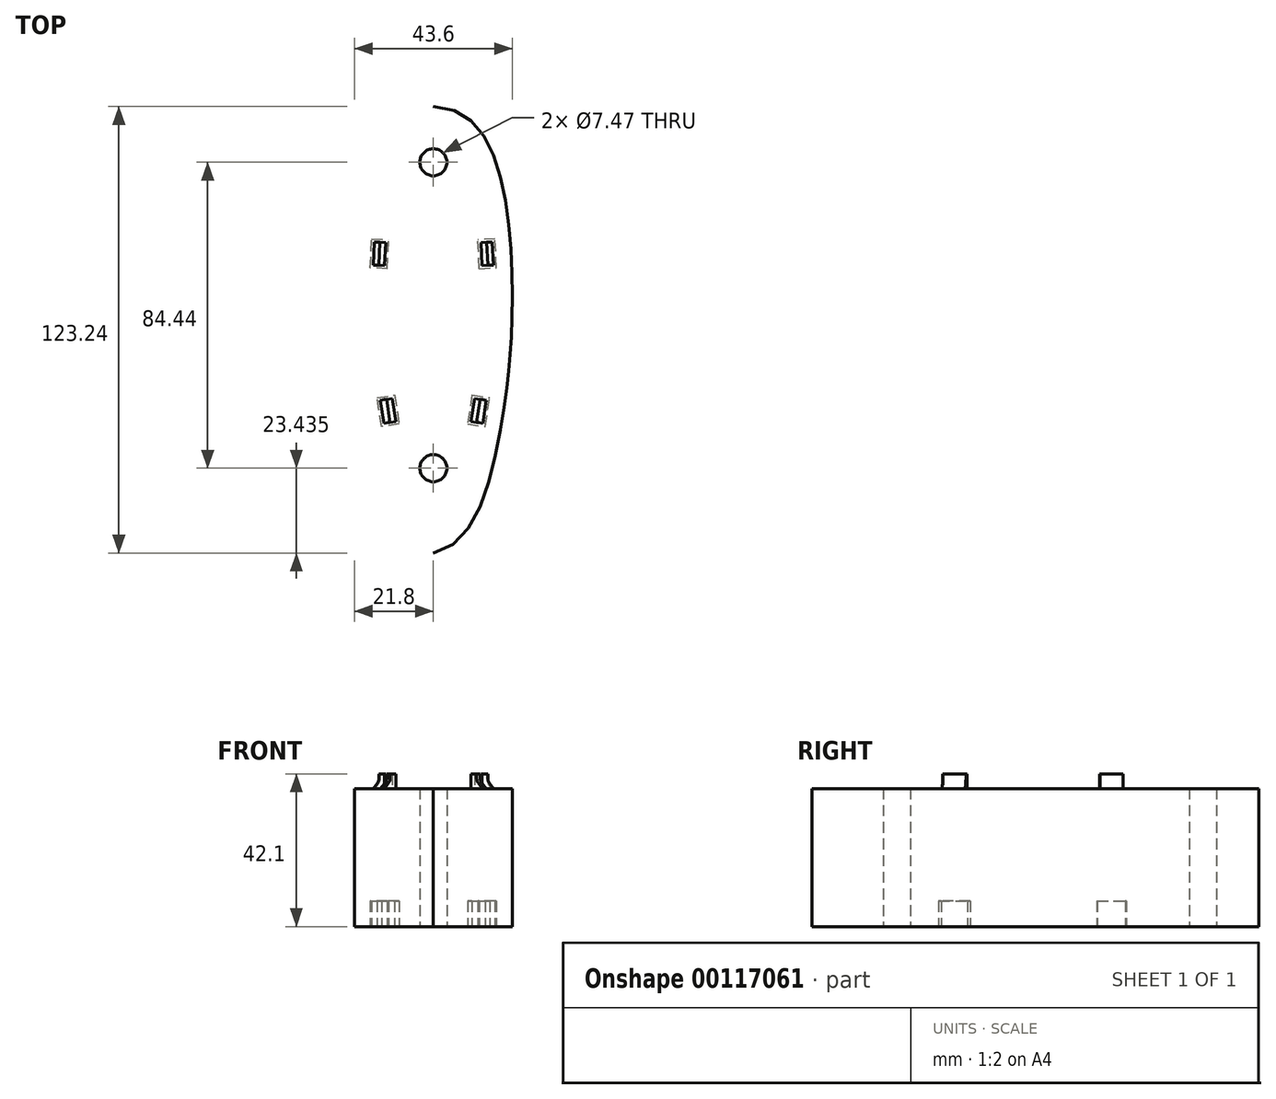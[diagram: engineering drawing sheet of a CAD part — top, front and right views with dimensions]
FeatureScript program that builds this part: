
annotation { "Feature Type Name" : "Feature", "Feature Type Description" : "" }
export const myFeature = defineFeature(function(context is Context, id is Id, definition is map)
    precondition{}
    {
        {
            var Q0;
            Q0=qCreatedBy(makeId("Top.planeOp"),FACE);
            var sketch = newSketch(context, id + "F0", { "sketchPlane" : qUnion([Q0])});
            skPoint(sketch, "E0", {"position": v(0, -61.62) * mm});
            skPoint(sketch, "E1", {"position": v(0, 61.62) * mm});
            skLineSegment(sketch, "E2", {"start": v(0, 71.88) * mm, "end": v(0, 61.62) * mm, "construction": true});
            skLineSegment(sketch, "E3", {"start": v(0, -61.62) * mm, "end": v(0, -68.33) * mm, "construction": true});
            skLineSegment(sketch, "E4", {"start": v(0, 61.62) * mm, "end": v(0, -61.62) * mm, "construction": true});
            skLineSegment(sketch, "E5", {"start": v(-21.58, 0) * mm, "end": v(21.58, 0) * mm, "construction": true});
            skSolve(sketch);
        }
        {
            var Q0;
            Q0=qCreatedBy(makeId("Top.planeOp"),FACE);
            var sketch = newSketch(context, id + "F1", { "sketchPlane" : qUnion([Q0])});
            skPoint(sketch, "E6.0", {"position": v(0, -61.62) * mm});
            skPoint(sketch, "E7.0", {"position": v(-21.58, 0) * mm});
            skPoint(sketch, "E8.0", {"position": v(0, 61.62) * mm});
            skPoint(sketch, "E9.0", {"position": v(21.58, 0) * mm});
            skFitSpline(sketch, "E10", {"points": [v(0, 61.62) * mm, v(-18.98, 40.1) * mm, v(-21.58, 0) * mm, v(-18.86, -25.18) * mm, v(0, -61.62) * mm], "startDerivative": vector(-149.62, -2.8) * mm, "endDerivative": vector(137.56, -24.42) * mm});
            skLineSegment(sketch, "E11.0", {"start": v(0, 61.62) * mm, "end": v(0, -61.62) * mm, "construction": true});
            skFitSpline(sketch, "E12.MirrorCS", {"points": [v(0, 61.62) * mm, v(18.98, 40.1) * mm, v(21.58, 0) * mm, v(18.86, -25.18) * mm, v(0, -61.62) * mm], "startDerivative": vector(149.62, -2.8) * mm, "endDerivative": vector(-137.56, -24.42) * mm});
            skCircle(sketch, "E13", {"center": v(0, 46.26) * mm, "radius": 2.94 * mm});
            skLineSegment(sketch, "E14", {"start": v(0, 49.2) * mm, "end": v(0, 61.62) * mm, "construction": true});
            skCircle(sketch, "E15", {"center": v(0, -38.18) * mm, "radius": 2.94 * mm});
            skLineSegment(sketch, "E16", {"start": v(0, -61.62) * mm, "end": v(0, -41.12) * mm, "construction": true});
            skFitSpline(sketch, "E17.0", {"points": [v(0.1, 56.52) * mm, v(-1.07, 56.5) * mm, v(-2.58, 56.27) * mm, v(-4.26, 55.69) * mm, v(-5.4, 55.12) * mm, v(-6.45, 54.4) * mm, v(-7.79, 53.23) * mm, v(-9.34, 51.35) * mm, v(-11, 48.38) * mm, v(-12.44, 44.8) * mm, v(-13.42, 41.44) * mm, v(-14.1, 38.58) * mm, v(-14.72, 35.65) * mm, v(-15.35, 31.88) * mm, v(-16.11, 25.7) * mm, v(-16.53, 19.45) * mm, v(-16.7, 13.37) * mm, v(-16.71, 8.96) * mm, v(-16.66, 5.46) * mm, v(-16.58, 2.8) * mm, v(-16.51, 0.86) * mm, v(-16.43, -0.98) * mm, v(-16.32, -3.32) * mm, v(-16.15, -6.08) * mm, v(-15.88, -9.27) * mm, v(-15.55, -12.48) * mm, v(-15.13, -15.85) * mm, v(-14.6, -19.52) * mm, v(-14.06, -22.95) * mm, v(-13.56, -25.98) * mm, v(-13, -29.14) * mm, v(-12.22, -33.28) * mm, v(-11.05, -38.32) * mm, v(-9.62, -43.18) * mm, v(-7.9, -47.62) * mm, v(-5.9, -51.36) * mm, v(-4.07, -53.7) * mm, v(-2.58, -55.03) * mm, v(-1.47, -55.78) * mm, v(-0.34, -56.3) * mm, v(0.46, -56.52) * mm, v(0.9, -56.6) * mm], "construction": true});
            skFitSpline(sketch, "E18.0", {"points": [v(-0.1, 56.52) * mm, v(1.07, 56.5) * mm, v(2.58, 56.27) * mm, v(4.26, 55.69) * mm, v(5.4, 55.12) * mm, v(6.45, 54.4) * mm, v(7.79, 53.23) * mm, v(9.34, 51.35) * mm, v(11, 48.38) * mm, v(12.44, 44.8) * mm, v(13.42, 41.44) * mm, v(14.1, 38.58) * mm, v(14.72, 35.65) * mm, v(15.35, 31.88) * mm, v(16.11, 25.7) * mm, v(16.53, 19.45) * mm, v(16.7, 13.37) * mm, v(16.71, 8.96) * mm, v(16.66, 5.46) * mm, v(16.58, 2.8) * mm, v(16.51, 0.86) * mm, v(16.43, -0.98) * mm, v(16.32, -3.32) * mm, v(16.15, -6.08) * mm, v(15.88, -9.27) * mm, v(15.55, -12.48) * mm, v(15.13, -15.85) * mm, v(14.6, -19.52) * mm, v(14.06, -22.95) * mm, v(13.56, -25.98) * mm, v(13, -29.14) * mm, v(12.22, -33.28) * mm, v(11.05, -38.32) * mm, v(9.62, -43.18) * mm, v(7.9, -47.62) * mm, v(5.9, -51.36) * mm, v(4.07, -53.7) * mm, v(2.58, -55.03) * mm, v(1.47, -55.78) * mm, v(0.34, -56.3) * mm, v(-0.46, -56.52) * mm, v(-0.9, -56.6) * mm], "construction": true});
            skLineSegment(sketch, "E19", {"start": v(-13.46, 17.73) * mm, "end": v(13.46, 17.73) * mm, "construction": true});
            skLineSegment(sketch, "E20", {"start": v(-11.32, -18.93) * mm, "end": v(11.32, -18.93) * mm, "construction": true});
            skPoint(sketch, "E21", {"position": v(0, -18.93) * mm});
            skLineSegment(sketch, "E22", {"start": v(-10.36, -25.3) * mm, "end": v(10.36, -25.3) * mm, "construction": true});
            skPoint(sketch, "E23", {"position": v(0, -25.3) * mm});
            skLineSegment(sketch, "E24", {"start": v(-11.32, -18.93) * mm, "end": v(-10.36, -25.3) * mm});
            skLineSegment(sketch, "E25", {"start": v(-11.32, -18.93) * mm, "end": v(-14.6, -19.42) * mm});
            skLineSegment(sketch, "E26", {"start": v(-14.6, -19.42) * mm, "end": v(-13.64, -25.8) * mm});
            skLineSegment(sketch, "E27", {"start": v(-15.51, -18.75) * mm, "end": v(-10.65, -18.02) * mm});
            skLineSegment(sketch, "E28", {"start": v(-14.31, -26.7) * mm, "end": v(-15.51, -18.75) * mm});
            skLineSegment(sketch, "E29", {"start": v(-10.65, -18.02) * mm, "end": v(-15.51, -18.75) * mm});
            skLineSegment(sketch, "E30", {"start": v(-10.65, -18.02) * mm, "end": v(-9.45, -25.97) * mm});
            skLineSegment(sketch, "E31", {"start": v(-9.45, -25.97) * mm, "end": v(-14.31, -26.7) * mm});
            skLineSegment(sketch, "E32.MirrorCS", {"start": v(10.65, -18.02) * mm, "end": v(9.45, -25.97) * mm});
            skLineSegment(sketch, "E33.MirrorCS", {"start": v(11.32, -18.93) * mm, "end": v(10.36, -25.3) * mm});
            skLineSegment(sketch, "E34.MirrorCS", {"start": v(9.45, -25.97) * mm, "end": v(14.31, -26.7) * mm});
            skLineSegment(sketch, "E35.MirrorCS", {"start": v(10.36, -25.3) * mm, "end": v(13.64, -25.8) * mm});
            skLineSegment(sketch, "E36.MirrorCS", {"start": v(11.32, -18.93) * mm, "end": v(14.6, -19.42) * mm});
            skLineSegment(sketch, "E37.MirrorCS", {"start": v(10.65, -18.02) * mm, "end": v(15.51, -18.75) * mm});
            skLineSegment(sketch, "E38.MirrorCS", {"start": v(14.31, -26.7) * mm, "end": v(15.51, -18.75) * mm});
            skLineSegment(sketch, "E39.MirrorCS", {"start": v(14.6, -19.42) * mm, "end": v(13.64, -25.8) * mm});
            skPoint(sketch, "E40", {"position": v(0, 17.73) * mm});
            skLineSegment(sketch, "E41", {"start": v(-13.15, 24.1) * mm, "end": v(13.15, 24.1) * mm, "construction": true});
            skPoint(sketch, "E42", {"position": v(0, 24.1) * mm});
            skLineSegment(sketch, "E43", {"start": v(-13.46, 17.73) * mm, "end": v(-13.15, 24.1) * mm});
            skLineSegment(sketch, "E44", {"start": v(-13.46, 17.73) * mm, "end": v(-16.55, 17.88) * mm});
            skLineSegment(sketch, "E45", {"start": v(-16.55, 17.88) * mm, "end": v(-16.25, 24.24) * mm});
            skLineSegment(sketch, "E46", {"start": v(-16.25, 24.24) * mm, "end": v(-13.15, 24.1) * mm});
            skLineSegment(sketch, "E47.0", {"start": v(-17.01, 25.07) * mm, "end": v(-12.32, 24.85) * mm});
            skLineSegment(sketch, "E47.1", {"start": v(-17.39, 17.11) * mm, "end": v(-17.01, 25.07) * mm});
            skLineSegment(sketch, "E47.2", {"start": v(-12.7, 16.9) * mm, "end": v(-17.39, 17.11) * mm});
            skLineSegment(sketch, "E47.3", {"start": v(-12.7, 16.9) * mm, "end": v(-12.32, 24.85) * mm});
            skLineSegment(sketch, "E48.MirrorCS", {"start": v(13.46, 17.73) * mm, "end": v(13.15, 24.1) * mm});
            skLineSegment(sketch, "E49.MirrorCS", {"start": v(12.7, 16.9) * mm, "end": v(12.32, 24.85) * mm});
            skLineSegment(sketch, "E50.MirrorCS", {"start": v(17.01, 25.07) * mm, "end": v(12.32, 24.85) * mm});
            skLineSegment(sketch, "E51.MirrorCS", {"start": v(16.25, 24.24) * mm, "end": v(13.15, 24.1) * mm});
            skLineSegment(sketch, "E52.MirrorCS", {"start": v(17.39, 17.11) * mm, "end": v(17.01, 25.07) * mm});
            skLineSegment(sketch, "E53.MirrorCS", {"start": v(16.55, 17.88) * mm, "end": v(16.25, 24.24) * mm});
            skLineSegment(sketch, "E54.MirrorCS", {"start": v(13.46, 17.73) * mm, "end": v(16.55, 17.88) * mm});
            skLineSegment(sketch, "E55.MirrorCS", {"start": v(12.7, 16.9) * mm, "end": v(17.39, 17.11) * mm});
            skPoint(sketch, "E56", {"position": v(0, -35.25) * mm});
            skPoint(sketch, "E57", {"position": v(0, 43.32) * mm});
            skCircle(sketch, "E58.0", {"center": v(0, 46.26) * mm, "radius": 3.74 * mm});
            skCircle(sketch, "E59.0", {"center": v(0, -38.18) * mm, "radius": 3.74 * mm});
            skLineSegment(sketch, "E60", {"start": v(-13.64, -25.8) * mm, "end": v(-10.36, -25.3) * mm});
            skSolve(sketch);
        }
        {
            var Q0;
            Q0=makeQuery(id+"F1.imprint","IMPRINT",FACE,{"disambiguationData":[TD([[makeQuery(id+"F1.imprint","IMPRINT",EDGE,{"derivedFrom":sQuery(id+"F1.wireOp",EDGE,"E10")}),1.0]])]});
            var Q1;
            Q1=makeQuery(id+"F1.imprint","IMPRINT",FACE,{"disambiguationData":[TD([[makeQuery(id+"F1.imprint","IMPRINT",EDGE,{"derivedFrom":sQuery(id+"F1.wireOp",EDGE,"E43")}),1.0]])]});
            var Q2;
            Q2=makeQuery(id+"F1.imprint","IMPRINT",FACE,{"disambiguationData":[TD([[makeQuery(id+"F1.imprint","IMPRINT",EDGE,{"derivedFrom":sQuery(id+"F1.wireOp",EDGE,"E43")}),-1.0]])]});
            var Q3;
            Q3=makeQuery(id+"F1.imprint","IMPRINT",FACE,{"disambiguationData":[TD([[makeQuery(id+"F1.imprint","IMPRINT",EDGE,{"derivedFrom":sQuery(id+"F1.wireOp",EDGE,"E48.MirrorCS")}),1.0]])]});
            var Q4;
            Q4=makeQuery(id+"F1.imprint","IMPRINT",FACE,{"disambiguationData":[TD([[makeQuery(id+"F1.imprint","IMPRINT",EDGE,{"derivedFrom":sQuery(id+"F1.wireOp",EDGE,"E48.MirrorCS")}),-1.0]])]});
            var Q5;
            {var subQ0=sQuery(id+"F1.wireOp",EDGE,"E33.MirrorCS");Q5=makeQuery(id+"F1.imprint","IMPRINT",FACE,{"disambiguationData":[TD([[makeQuery(id+"F1.imprint","IMPRINT",EDGE,{"derivedFrom":subQ0}),1.0]])]});}
            var Q6;
            Q6=makeQuery(id+"F1.imprint","IMPRINT",FACE,{"disambiguationData":[TD([[makeQuery(id+"F1.imprint","IMPRINT",EDGE,{"derivedFrom":sQuery(id+"F1.wireOp",EDGE,"E32.MirrorCS")}),1.0]])]});
            var Q7;
            {var subQ2=sQuery(id+"F1.wireOp",EDGE,"E24");Q7=makeQuery(id+"F1.imprint","IMPRINT",FACE,{"disambiguationData":[TD([[makeQuery(id+"F1.imprint","IMPRINT",EDGE,{"derivedFrom":subQ2}),1.0]])]});}
            var Q8;
            Q8=makeQuery(id+"F1.imprint","IMPRINT",FACE,{"disambiguationData":[TD([[makeQuery(id+"F1.imprint","IMPRINT",EDGE,{"derivedFrom":sQuery(id+"F1.wireOp",EDGE,"E28")}),-1.0]])]});
            var Q9;
            Q9=makeQuery(id+"F1.imprint","IMPRINT",FACE,{"disambiguationData":[TD([[makeQuery(id+"F1.imprint","IMPRINT",EDGE,{"derivedFrom":sQuery(id+"F1.wireOp",EDGE,"E24")}),-1.0]])]});
            extrude(context, id + "F2", {"entities" : qUnion([Q0, Q1, Q2, Q3, Q4, Q5, Q6, Q7, Q8, Q9]), "depth" : 38.1 * mm});
        }
        {
            var Q0;
            Q0=makeQuery(id+"F2.opExtrude","CAP_FACE",FACE,{"disambiguationData":[OSD([sQuery(id+"F1.wireOp",EDGE,"E10"),sQuery(id+"F1.wireOp",EDGE,"E12.MirrorCS"),sQuery(id+"F1.wireOp",EDGE,"E13"),sQuery(id+"F1.wireOp",EDGE,"E15")])],"isStart":false});
            var sketch = newSketch(context, id + "F3", { "sketchPlane" : qUnion([Q0])});
            skLineSegment(sketch, "E61.0", {"start": v(-13.46, 17.73) * mm, "end": v(-16.55, 17.88) * mm});
            skLineSegment(sketch, "E62.0", {"start": v(-13.46, 17.73) * mm, "end": v(-13.15, 24.1) * mm});
            skLineSegment(sketch, "E63.0", {"start": v(-16.55, 17.88) * mm, "end": v(-16.25, 24.24) * mm});
            skLineSegment(sketch, "E64.0", {"start": v(-16.25, 24.24) * mm, "end": v(-13.15, 24.1) * mm});
            skLineSegment(sketch, "E65.0", {"start": v(13.46, 17.73) * mm, "end": v(16.55, 17.88) * mm});
            skLineSegment(sketch, "E66.0", {"start": v(13.46, 17.73) * mm, "end": v(13.15, 24.1) * mm});
            skLineSegment(sketch, "E67.0", {"start": v(16.55, 17.88) * mm, "end": v(16.25, 24.24) * mm});
            skLineSegment(sketch, "E68.0", {"start": v(16.25, 24.24) * mm, "end": v(13.15, 24.1) * mm});
            skLineSegment(sketch, "E69.0", {"start": v(-11.32, -18.93) * mm, "end": v(-10.36, -25.3) * mm});
            skLineSegment(sketch, "E70.0", {"start": v(-14.6, -19.42) * mm, "end": v(-13.64, -25.8) * mm});
            skLineSegment(sketch, "E71.0", {"start": v(-11.32, -18.93) * mm, "end": v(-14.6, -19.42) * mm});
            skLineSegment(sketch, "E72.0", {"start": v(11.32, -18.93) * mm, "end": v(14.6, -19.42) * mm});
            skLineSegment(sketch, "E73.0", {"start": v(11.32, -18.93) * mm, "end": v(10.36, -25.3) * mm});
            skLineSegment(sketch, "E74.0", {"start": v(10.36, -25.3) * mm, "end": v(13.64, -25.8) * mm});
            skLineSegment(sketch, "E75.0", {"start": v(14.6, -19.42) * mm, "end": v(13.64, -25.8) * mm});
            skLineSegment(sketch, "E76.0", {"start": v(-12.5, 16.68) * mm, "end": v(-12.1, 25.04) * mm});
            skLineSegment(sketch, "E76.1", {"start": v(-12.5, 16.68) * mm, "end": v(-17.6, 16.92) * mm});
            skLineSegment(sketch, "E76.2", {"start": v(-17.6, 16.92) * mm, "end": v(-17.2, 25.28) * mm});
            skLineSegment(sketch, "E76.3", {"start": v(-17.2, 25.28) * mm, "end": v(-12.1, 25.04) * mm});
            skLineSegment(sketch, "E77.0", {"start": v(17.2, 25.28) * mm, "end": v(12.1, 25.04) * mm});
            skLineSegment(sketch, "E77.1", {"start": v(17.6, 16.92) * mm, "end": v(17.2, 25.28) * mm});
            skLineSegment(sketch, "E77.2", {"start": v(12.5, 16.68) * mm, "end": v(17.6, 16.92) * mm});
            skLineSegment(sketch, "E77.3", {"start": v(12.5, 16.68) * mm, "end": v(12.1, 25.04) * mm});
            skFitSpline(sketch, "E78.0", {"points": [v(-0.87, -56.7) * mm, v(-0.44, -56.62) * mm, v(0.37, -56.4) * mm, v(1.52, -55.87) * mm, v(2.65, -55.11) * mm, v(4.15, -53.77) * mm, v(5.99, -51.42) * mm, v(8, -47.66) * mm, v(9.72, -43.21) * mm, v(11.15, -38.34) * mm, v(12.32, -33.3) * mm, v(13.1, -29.16) * mm, v(13.65, -26) * mm, v(14.15, -22.97) * mm, v(14.7, -19.54) * mm, v(15.22, -15.86) * mm, v(15.65, -12.49) * mm, v(15.98, -9.28) * mm, v(16.25, -6.1) * mm, v(16.42, -3.33) * mm, v(16.53, -0.98) * mm, v(16.61, 0.86) * mm, v(16.68, 2.79) * mm, v(16.76, 5.46) * mm, v(16.81, 8.96) * mm, v(16.8, 13.37) * mm, v(16.63, 19.46) * mm, v(16.21, 25.71) * mm, v(15.45, 31.9) * mm, v(14.81, 35.67) * mm, v(14.2, 38.6) * mm, v(13.52, 41.47) * mm, v(12.53, 44.84) * mm, v(11.1, 48.43) * mm, v(9.42, 51.4) * mm, v(7.55, 53.68) * mm, v(5.83, 55) * mm, v(4.3, 55.78) * mm, v(2.6, 56.37) * mm, v(1.08, 56.6) * mm, v(-0.1, 56.62) * mm]});
            skFitSpline(sketch, "E78.1", {"points": [v(0.1, 56.62) * mm, v(-1.08, 56.6) * mm, v(-2.6, 56.37) * mm, v(-4.3, 55.78) * mm, v(-5.83, 55) * mm, v(-7.55, 53.68) * mm, v(-9.42, 51.4) * mm, v(-11.1, 48.43) * mm, v(-12.53, 44.84) * mm, v(-13.52, 41.47) * mm, v(-14.2, 38.6) * mm, v(-14.81, 35.67) * mm, v(-15.45, 31.9) * mm, v(-16.21, 25.71) * mm, v(-16.63, 19.46) * mm, v(-16.8, 13.37) * mm, v(-16.81, 8.96) * mm, v(-16.76, 5.46) * mm, v(-16.68, 2.79) * mm, v(-16.61, 0.86) * mm, v(-16.53, -0.98) * mm, v(-16.42, -3.33) * mm, v(-16.25, -6.1) * mm, v(-15.98, -9.28) * mm, v(-15.65, -12.49) * mm, v(-15.22, -15.86) * mm, v(-14.7, -19.54) * mm, v(-14.15, -22.97) * mm, v(-13.65, -26) * mm, v(-13.1, -29.16) * mm, v(-12.32, -33.3) * mm, v(-11.15, -38.34) * mm, v(-9.72, -43.21) * mm, v(-8, -47.66) * mm, v(-5.99, -51.42) * mm, v(-4.15, -53.77) * mm, v(-2.65, -55.11) * mm, v(-1.52, -55.87) * mm, v(-0.37, -56.4) * mm, v(0.44, -56.62) * mm, v(0.87, -56.7) * mm]});
            skLineSegment(sketch, "E79.0", {"start": v(-13.64, -25.8) * mm, "end": v(-10.36, -25.3) * mm});
            skLineSegment(sketch, "E80.0", {"start": v(-10.48, -17.8) * mm, "end": v(-15.74, -18.59) * mm});
            skLineSegment(sketch, "E80.1", {"start": v(-10.48, -17.8) * mm, "end": v(-9.22, -26.14) * mm});
            skLineSegment(sketch, "E80.2", {"start": v(-14.48, -26.93) * mm, "end": v(-9.22, -26.14) * mm});
            skLineSegment(sketch, "E80.3", {"start": v(-15.74, -18.59) * mm, "end": v(-14.48, -26.93) * mm});
            skLineSegment(sketch, "E81.0", {"start": v(10.48, -17.8) * mm, "end": v(9.22, -26.14) * mm});
            skLineSegment(sketch, "E81.1", {"start": v(10.48, -17.8) * mm, "end": v(15.74, -18.59) * mm});
            skLineSegment(sketch, "E81.2", {"start": v(15.74, -18.59) * mm, "end": v(14.48, -26.93) * mm});
            skLineSegment(sketch, "E81.3", {"start": v(9.22, -26.14) * mm, "end": v(14.48, -26.93) * mm});
            skSolve(sketch);
        }
        {
            var Q0;
            {var subQ2=sQuery(id+"F3.wireOp",EDGE,"E69.0");Q0=makeQuery(id+"F3.imprint","IMPRINT",FACE,{"disambiguationData":[TD([[makeQuery(id+"F3.imprint","IMPRINT",EDGE,{"derivedFrom":subQ2}),-1.0]])]});}
            var Q1;
            Q1=makeQuery(id+"F3.imprint","IMPRINT",FACE,{"disambiguationData":[TD([[makeQuery(id+"F3.imprint","IMPRINT",EDGE,{"derivedFrom":sQuery(id+"F3.wireOp",EDGE,"E72.0")}),-1.0]])]});
            var Q2;
            Q2=makeQuery(id+"F3.imprint","IMPRINT",FACE,{"disambiguationData":[TD([[makeQuery(id+"F3.imprint","IMPRINT",EDGE,{"derivedFrom":sQuery(id+"F3.wireOp",EDGE,"E65.0")}),1.0]])]});
            var Q3;
            Q3=makeQuery(id+"F3.imprint","IMPRINT",FACE,{"disambiguationData":[TD([[makeQuery(id+"F3.imprint","IMPRINT",EDGE,{"derivedFrom":sQuery(id+"F3.wireOp",EDGE,"E61.0")}),-1.0]])]});
            extrude(context, id + "F4", {"entities" : qUnion([Q0, Q1, Q2, Q3]), "operationType" : NewBodyOperationType.ADD, "depth" : 4 * mm});
        }
        {
            var Q0;
            Q0=makeQuery(id+"F4.opExtrude","SWEPT_FACE",FACE,{"disambiguationData":[OSD([sQuery(id+"F3.wireOp",EDGE,"E79.0")])]});
            var sketch = newSketch(context, id + "F5", { "sketchPlane" : qUnion([Q0])});
            skLineSegment(sketch, "E82", {"start": v(-17.33, 38.1) * mm, "end": v(-15.6, 40.1) * mm});
            skPoint(sketch, "E82.endSnap0", {"position": v(-17.33, 40.1) * mm});
            skLineSegment(sketch, "E83", {"start": v(-15.6, 40.1) * mm, "end": v(-15.6, 42.1) * mm});
            skSolve(sketch);
        }
        {
            var Q0;
            Q0=makeQuery(id+"F5.imprint","IMPRINT",FACE,{"disambiguationData":[TD([[makeQuery(id+"F5.imprint","IMPRINT",EDGE,{"derivedFrom":sQuery(id+"F5.wireOp",EDGE,"E82")}),1.0]])]});
            extrude(context, id + "F6", {"entities" : qUnion([Q0]), "operationType" : NewBodyOperationType.REMOVE, "endBound" : BoundingType.UP_TO_NEXT, "oppositeDirection" : true, "depth" : 25 * mm});
        }
        {
            var Q0;
            Q0=makeQuery(id+"F4.opExtrude","SWEPT_FACE",FACE,{"disambiguationData":[OSD([sQuery(id+"F3.wireOp",EDGE,"E61.0")])]});
            var sketch = newSketch(context, id + "F7", { "sketchPlane" : qUnion([Q0])});
            skLineSegment(sketch, "E84", {"start": v(-15.86, 42.1) * mm, "end": v(-15.86, 40.1) * mm});
            skPoint(sketch, "E84.endSnap0", {"position": v(-17.38, 40.1) * mm});
            skLineSegment(sketch, "E85", {"start": v(-15.86, 40.1) * mm, "end": v(-17.38, 38.1) * mm});
            skSolve(sketch);
        }
        {
            var Q0;
            {var subQ0=sQuery(id+"F7.wireOp",EDGE,"E84");Q0=makeQuery(id+"F7.imprint","IMPRINT",FACE,{"disambiguationData":[TD([[makeQuery(id+"F7.imprint","IMPRINT",EDGE,{"derivedFrom":subQ0}),-1.0]])]});}
            extrude(context, id + "F8", {"entities" : qUnion([Q0]), "operationType" : NewBodyOperationType.REMOVE, "endBound" : BoundingType.UP_TO_NEXT, "oppositeDirection" : true, "depth" : 25 * mm});
        }
        {
            var Q0;
            Q0=makeQuery(id+"F4.opExtrude","SWEPT_FACE",FACE,{"disambiguationData":[OSD([sQuery(id+"F3.wireOp",EDGE,"E65.0")])]});
            var sketch = newSketch(context, id + "F9", { "sketchPlane" : qUnion([Q0])});
            skPoint(sketch, "E86.endSnap0", {"position": v(17.38, 40.1) * mm});
            skLineSegment(sketch, "E87", {"start": v(15.86, 40.1) * mm, "end": v(17.38, 38.1) * mm});
            skLineSegment(sketch, "E88", {"start": v(15.86, 40.1) * mm, "end": v(15.86, 42.1) * mm});
            skSolve(sketch);
        }
        {
            var Q0;
            Q0=makeQuery(id+"F9.imprint","IMPRINT",FACE,{"disambiguationData":[TD([[makeQuery(id+"F9.imprint","IMPRINT",EDGE,{"derivedFrom":sQuery(id+"F9.wireOp",EDGE,"E87")}),1.0]])]});
            extrude(context, id + "F10", {"entities" : qUnion([Q0]), "operationType" : NewBodyOperationType.REMOVE, "endBound" : BoundingType.UP_TO_NEXT, "oppositeDirection" : true, "depth" : 25 * mm});
        }
        {
            var Q0;
            Q0=makeQuery(id+"F4.opExtrude","SWEPT_FACE",FACE,{"disambiguationData":[OSD([sQuery(id+"F3.wireOp",EDGE,"E74.0")])]});
            var sketch = newSketch(context, id + "F11", { "sketchPlane" : qUnion([Q0])});
            skLineSegment(sketch, "E89", {"start": v(15.6, 42.1) * mm, "end": v(15.6, 40.1) * mm});
            skPoint(sketch, "E89.endSnap0", {"position": v(17.33, 40.1) * mm});
            skLineSegment(sketch, "E90", {"start": v(15.6, 40.1) * mm, "end": v(17.33, 38.1) * mm});
            skSolve(sketch);
        }
        {
            var Q0;
            {var subQ0=sQuery(id+"F11.wireOp",EDGE,"E89");Q0=makeQuery(id+"F11.imprint","IMPRINT",FACE,{"disambiguationData":[TD([[makeQuery(id+"F11.imprint","IMPRINT",EDGE,{"derivedFrom":subQ0}),1.0]])]});}
            extrude(context, id + "F12", {"entities" : qUnion([Q0]), "operationType" : NewBodyOperationType.REMOVE, "endBound" : BoundingType.UP_TO_NEXT, "oppositeDirection" : true, "depth" : 25 * mm});
        }
        {
            var Q0;
            Q0=makeQuery(id+"F12.boolean.opBoolean","COPY",EDGE,{"derivedFrom":makeQuery(id+"F12.opExtrude","SWEPT_EDGE",EDGE,{"disambiguationData":[OSD([sQuery(id+"F11.wireOp",EDGE,"E89"),sQuery(id+"F11.wireOp",EDGE,"E90")])]})});
            var Q1;
            Q1=makeQuery(id+"F10.boolean.opBoolean","COPY",EDGE,{"derivedFrom":makeQuery(id+"F10.opExtrude","SWEPT_EDGE",EDGE,{"disambiguationData":[OSD([sQuery(id+"F9.wireOp",EDGE,"E86"),sQuery(id+"F9.wireOp",EDGE,"E87")])]})});
            var Q2;
            Q2=makeQuery(id+"F6.boolean.opBoolean","COPY",EDGE,{"derivedFrom":makeQuery(id+"F6.opExtrude","SWEPT_EDGE",EDGE,{"disambiguationData":[OSD([sQuery(id+"F5.wireOp",EDGE,"agZW1Fb0-rpwG-JZMk-Ovys-17qRohZJhtTW"),sQuery(id+"F5.wireOp",EDGE,"3uhhlt4D-7DlG-nJoX-9AjA-X0Z9LdCK7Rig")])]})});
            var Q3;
            Q3=makeQuery(id+"F8.boolean.opBoolean","COPY",EDGE,{"derivedFrom":makeQuery(id+"F8.opExtrude","SWEPT_EDGE",EDGE,{"disambiguationData":[OSD([sQuery(id+"F7.wireOp",EDGE,"E84"),sQuery(id+"F7.wireOp",EDGE,"E85")])]})});
            var Q4;
            Q4=makeQuery(id+"F6.boolean.opBoolean","COPY",EDGE,{"derivedFrom":makeQuery(id+"F6.opExtrude","SWEPT_EDGE",EDGE,{"disambiguationData":[OSD([sQuery(id+"F5.wireOp",EDGE,"E82"),sQuery(id+"F5.wireOp",EDGE,"E83")])]})});
            fillet(context, id + "F13", {"entities" : qUnion([Q0, Q1, Q2, Q3, Q4]), "radius" : 2.5 * mm, "tangentPropagation" : true, "allowEdgeOverflow" : false});
        }
        {
            var Q0;
            Q0=makeQuery(id+"F1.imprint","IMPRINT",FACE,{"disambiguationData":[TD([[makeQuery(id+"F1.imprint","IMPRINT",EDGE,{"derivedFrom":sQuery(id+"F1.wireOp",EDGE,"E48.MirrorCS")}),-1.0]])]});
            var Q1;
            Q1=makeQuery(id+"F1.imprint","IMPRINT",FACE,{"disambiguationData":[TD([[makeQuery(id+"F1.imprint","IMPRINT",EDGE,{"derivedFrom":sQuery(id+"F1.wireOp",EDGE,"E43")}),1.0]])]});
            var Q2;
            {var subQ0=sQuery(id+"F1.wireOp",EDGE,"E24");Q2=makeQuery(id+"F1.imprint","IMPRINT",FACE,{"disambiguationData":[TD([[makeQuery(id+"F1.imprint","IMPRINT",EDGE,{"derivedFrom":subQ0}),-1.0]])]});}
            var Q3;
            {var subQ0=sQuery(id+"F1.wireOp",EDGE,"E33.MirrorCS");Q3=makeQuery(id+"F1.imprint","IMPRINT",FACE,{"disambiguationData":[TD([[makeQuery(id+"F1.imprint","IMPRINT",EDGE,{"derivedFrom":subQ0}),1.0]])]});}
            var Q4;
            Q4=makeQuery(id+"F1.imprint","IMPRINT",FACE,{"disambiguationData":[TD([[makeQuery(id+"F1.imprint","IMPRINT",EDGE,{"derivedFrom":sQuery(id+"F1.wireOp",EDGE,"E48.MirrorCS")}),1.0]])]});
            var Q5;
            Q5=makeQuery(id+"F1.imprint","IMPRINT",FACE,{"disambiguationData":[TD([[makeQuery(id+"F1.imprint","IMPRINT",EDGE,{"derivedFrom":sQuery(id+"F1.wireOp",EDGE,"E43")}),-1.0]])]});
            var Q6;
            Q6=makeQuery(id+"F1.imprint","IMPRINT",FACE,{"disambiguationData":[TD([[makeQuery(id+"F1.imprint","IMPRINT",EDGE,{"derivedFrom":sQuery(id+"F1.wireOp",EDGE,"E32.MirrorCS")}),1.0]])]});
            var Q7;
            Q7=makeQuery(id+"F1.imprint","IMPRINT",FACE,{"disambiguationData":[TD([[makeQuery(id+"F1.imprint","IMPRINT",EDGE,{"derivedFrom":sQuery(id+"F1.wireOp",EDGE,"E24")}),1.0]])]});
            extrude(context, id + "F14", {"entities" : qUnion([Q0, Q1, Q2, Q3, Q4, Q5, Q6, Q7]), "operationType" : NewBodyOperationType.REMOVE, "depth" : 7 * mm});
        }
    });
